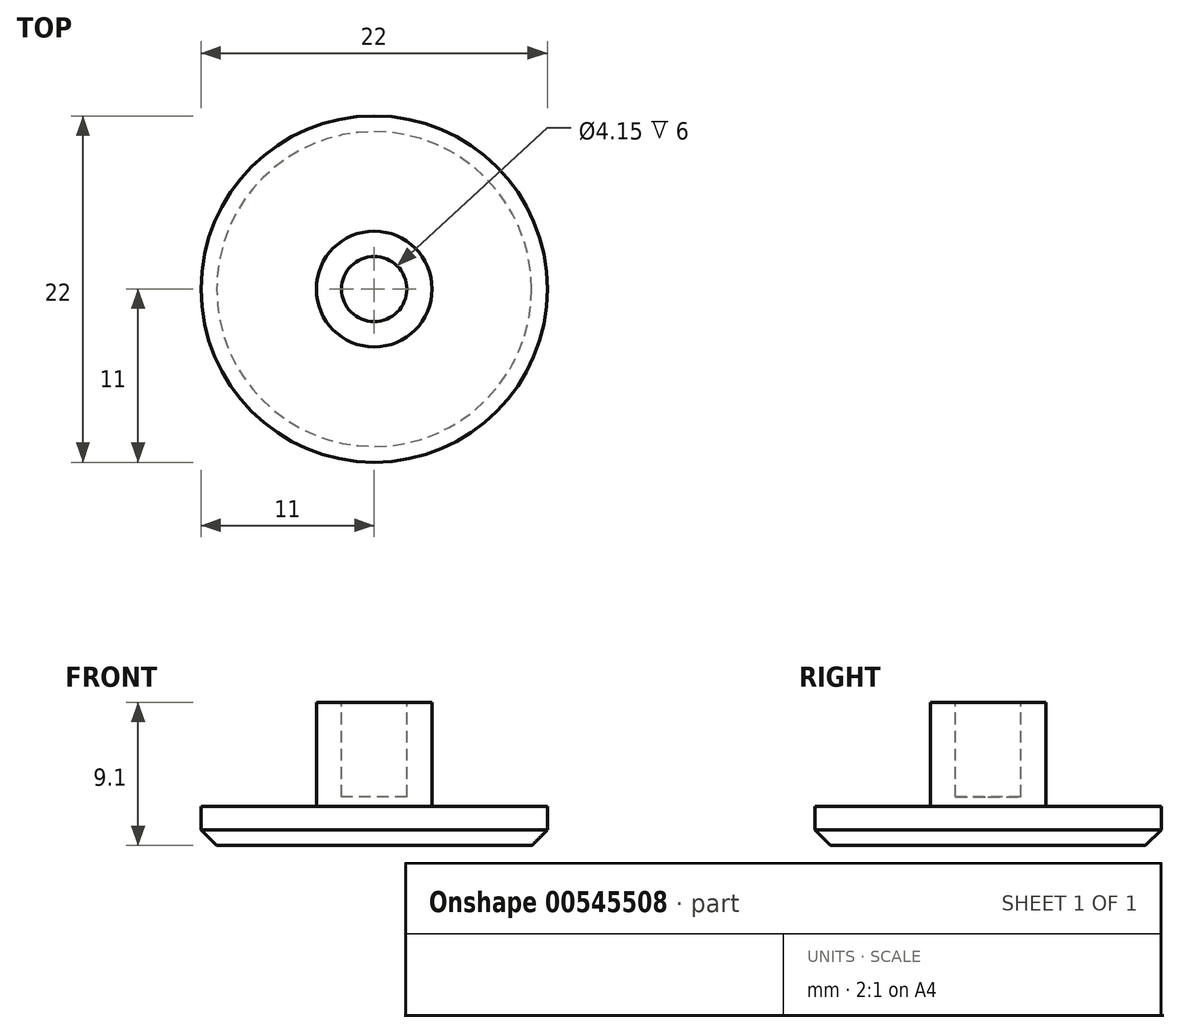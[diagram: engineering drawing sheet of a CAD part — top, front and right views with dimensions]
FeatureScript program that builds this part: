
annotation { "Feature Type Name" : "Feature", "Feature Type Description" : "" }
export const myFeature = defineFeature(function(context is Context, id is Id, definition is map)
    precondition{}
    {
        {
            var Q0;
            Q0=qCreatedBy(makeId("Top.planeOp"),FACE);
            var sketch = newSketch(context, id + "F0", { "sketchPlane" : qUnion([Q0])});
            skCircle(sketch, "E0", {"center": v(0, 0) * mm, "radius": 11 * mm});
            skSolve(sketch);
        }
        {
            var Q0;
            Q0=makeQuery(id+"F0.imprint","IMPRINT",FACE,{"disambiguationData":[TD([[makeQuery(id+"F0.imprint","IMPRINT",EDGE,{"derivedFrom":sQuery(id+"F0.wireOp",EDGE,"E0")}),1.0]])]});
            extrude(context, id + "F1", {"entities" : qUnion([Q0]), "depth" : 2.5 * mm, "offsetDistance" : 25 * mm});
        }
        {
            var Q0;
            Q0=makeQuery(id+"F1.opExtrude","CAP_EDGE",EDGE,{"disambiguationData":[OSD([sQuery(id+"F0.wireOp",EDGE,"E0")])],"isStart":true});
            chamfer(context, id + "F2", {"entities" : qUnion([Q0]), "chamferType" : ChamferType.OFFSET_ANGLE, "width" : 1 * mm, "oppositeDirection" : false, "angle" : 45 * degree, "tangentPropagation" : true});
        }
        {
            var Q0;
            Q0=makeQuery(id+"F1.opExtrude","CAP_FACE",FACE,{"disambiguationData":[OSD([sQuery(id+"F0.wireOp",EDGE,"E0")])],"isStart":false});
            var sketch = newSketch(context, id + "F3", { "sketchPlane" : qUnion([Q0])});
            skCircle(sketch, "E1", {"center": v(0, 0) * mm, "radius": 3.67 * mm});
            skSolve(sketch);
        }
        {
            var Q0;
            Q0=makeQuery(id+"F3.imprint","IMPRINT",FACE,{"disambiguationData":[TD([[makeQuery(id+"F3.imprint","IMPRINT",EDGE,{"derivedFrom":sQuery(id+"F3.wireOp",EDGE,"E1")}),1.0]])]});
            extrude(context, id + "F4", {"entities" : qUnion([Q0]), "operationType" : NewBodyOperationType.ADD, "depth" : 6.6 * mm, "offsetDistance" : 25 * mm});
        }
        {
            var Q0;
            Q0=makeQuery(id+"F4.opExtrude","CAP_FACE",FACE,{"disambiguationData":[OSD([sQuery(id+"F3.wireOp",EDGE,"E1")])],"isStart":false});
            var sketch = newSketch(context, id + "F5", { "sketchPlane" : qUnion([Q0])});
            skCircle(sketch, "E2", {"center": v(0, 0) * mm, "radius": 2.08 * mm});
            skSolve(sketch);
        }
        {
            var Q0;
            Q0=makeQuery(id+"F5.imprint","IMPRINT",FACE,{"disambiguationData":[TD([[makeQuery(id+"F5.imprint","IMPRINT",EDGE,{"derivedFrom":sQuery(id+"F5.wireOp",EDGE,"E2")}),1.0]])]});
            extrude(context, id + "F6", {"entities" : qUnion([Q0]), "operationType" : NewBodyOperationType.REMOVE, "oppositeDirection" : true, "depth" : 6 * mm, "offsetDistance" : 25 * mm});
        }
    });
